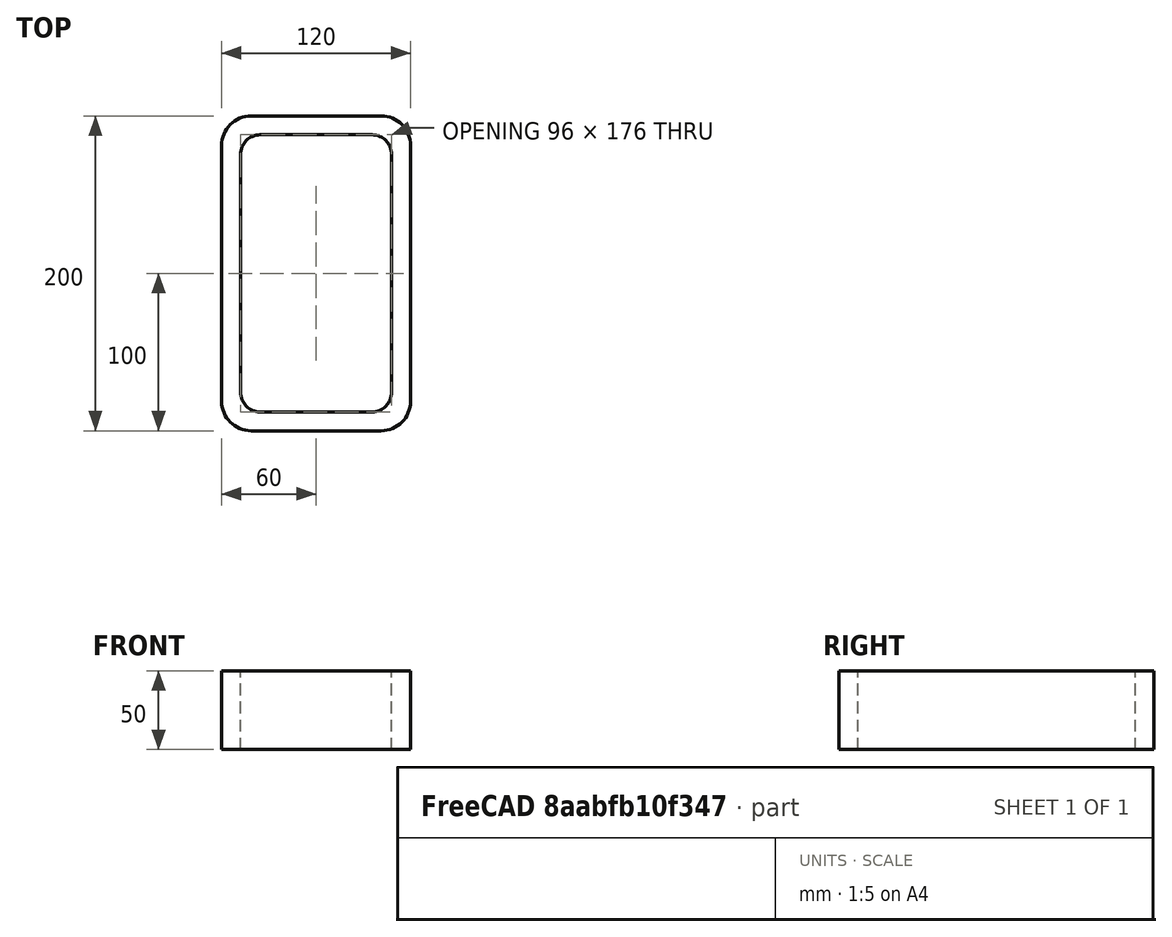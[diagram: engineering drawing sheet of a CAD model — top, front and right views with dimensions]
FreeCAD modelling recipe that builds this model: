
FCSTD DOCUMENT  (FreeCAD 0.15R4671 (Git))
Label: Rectangular hollow section 200x120x12 EN10219 S235JRH
License: All rights reserved
LicenseURL: http://en.wikipedia.org/wiki/All_rights_reserved
objects: Sketcher::SketchObject×1, Part::Extrusion×1
note: 2 computed .brp shape members not serialized (recipe doc carries the construction recipe); baked Part::Feature solids carry a one-line shape summary decoded from their .brp

FEATURE [Sketcher::SketchObject] Sketch
  sketch-geometry (16):
    g0: LineSegment StartX=-35.5 StartY=88 StartZ=0 EndX=35.5 EndY=88 EndZ=0
    g1: LineSegment StartX=48 StartY=75.5 StartZ=0 EndX=48 EndY=-75.5 EndZ=0
    g2: LineSegment StartX=35.5 StartY=-88 StartZ=0 EndX=-35.5 EndY=-88 EndZ=0
    g3: LineSegment StartX=-48 StartY=-75.5 StartZ=0 EndX=-48 EndY=75.5 EndZ=0
    g4: LineSegment StartX=-41.25 StartY=100 StartZ=0 EndX=41.25 EndY=100 EndZ=0
    g5: LineSegment StartX=60 StartY=81.25 StartZ=0 EndX=60 EndY=-81.25 EndZ=0
    g6: LineSegment StartX=41.25 StartY=-100 StartZ=0 EndX=-41.25 EndY=-100 EndZ=0
    g7: LineSegment StartX=-60 StartY=-81.25 StartZ=0 EndX=-60 EndY=81.25 EndZ=0
    g8: ArcOfCircle CenterX=-35.5 CenterY=75.5 CenterZ=0 NormalX=0 NormalY=0 NormalZ=1 Radius=12.5 StartAngle=1.5708 EndAngle=3.14159
    g9: ArcOfCircle CenterX=35.5 CenterY=75.5 CenterZ=0 NormalX=0 NormalY=0 NormalZ=1 Radius=12.5 StartAngle=0 EndAngle=1.5708
    g10: ArcOfCircle CenterX=35.5 CenterY=-75.5 CenterZ=0 NormalX=0 NormalY=0 NormalZ=1 Radius=12.5 StartAngle=4.71239 EndAngle=6.28319
    g11: ArcOfCircle CenterX=-35.5 CenterY=-75.5 CenterZ=0 NormalX=0 NormalY=0 NormalZ=1 Radius=12.5 StartAngle=3.14159 EndAngle=4.71239
    g12: ArcOfCircle CenterX=41.25 CenterY=81.25 CenterZ=0 NormalX=0 NormalY=0 NormalZ=1 Radius=18.75 StartAngle=0 EndAngle=1.5708
    g13: ArcOfCircle CenterX=41.25 CenterY=-81.25 CenterZ=0 NormalX=0 NormalY=0 NormalZ=1 Radius=18.75 StartAngle=4.71239 EndAngle=6.28319
    g14: ArcOfCircle CenterX=-41.25 CenterY=-81.25 CenterZ=0 NormalX=0 NormalY=0 NormalZ=1 Radius=18.75 StartAngle=3.14159 EndAngle=4.71239
    g15: ArcOfCircle CenterX=-41.25 CenterY=81.25 CenterZ=0 NormalX=0 NormalY=0 NormalZ=1 Radius=18.75 StartAngle=1.5708 EndAngle=3.14159
  constraints (36):
    c: Horizontal(g2)
    c: Vertical(g3)
    c: Horizontal(g6)
    c: Vertical(g7)
    c: Tangent(g3,g8) = 1.5708
    c: Tangent(g0,g8) = 1.5708
    c: Tangent(g0,g9) = 1.5708
    c: Tangent(g1,g9) = 1.5708
    c: Tangent(g1,g10) = 1.5708
    c: Tangent(g2,g10) = 1.5708
    c: Tangent(g2,g11) = 1.5708
    c: Tangent(g3,g11) = 1.5708
    c: Tangent(g4,g12) = 1.5708
    c: Tangent(g5,g12) = 1.5708
    c: Tangent(g5,g13) = 1.5708
    c: Tangent(g6,g13) = 1.5708
    c: Tangent(g6,g14) = 1.5708
    c: Tangent(g7,g14) = 1.5708
    c: Tangent(g7,g15) = 1.5708
    c: Tangent(g4,g15) = 1.5708
    c: Equal(g9,g8)
    c: Equal(g9,g11)
    c: Equal(g9,g10)
    c: Equal(g12,g15)
    c: Equal(g12,g14)
    c: Equal(g12,g13)
    c: Symmetric(g4,g6,g-1)
    c: Symmetric(g7,g5,g-2)
    c: DistanceY(g4,g6) = -200
    c: DistanceX(g7,g5) = 120
    c: Symmetric(g3,g1,g-2)
    c: Symmetric(g0,g2,g-1)
    c: DistanceY(g0,g4) = 12
    c: DistanceX(g5,g1) = -12
    c: Radius(g9) = 12.5
    c: Radius(g12) = 18.75
FEATURE [Part::Extrusion] Extrude  label="Rectangular hollow section 200x120x12 EN10219 S235JRH"
  Base = -> Sketch
  Dir = (0,0,50)
  Solid = true
